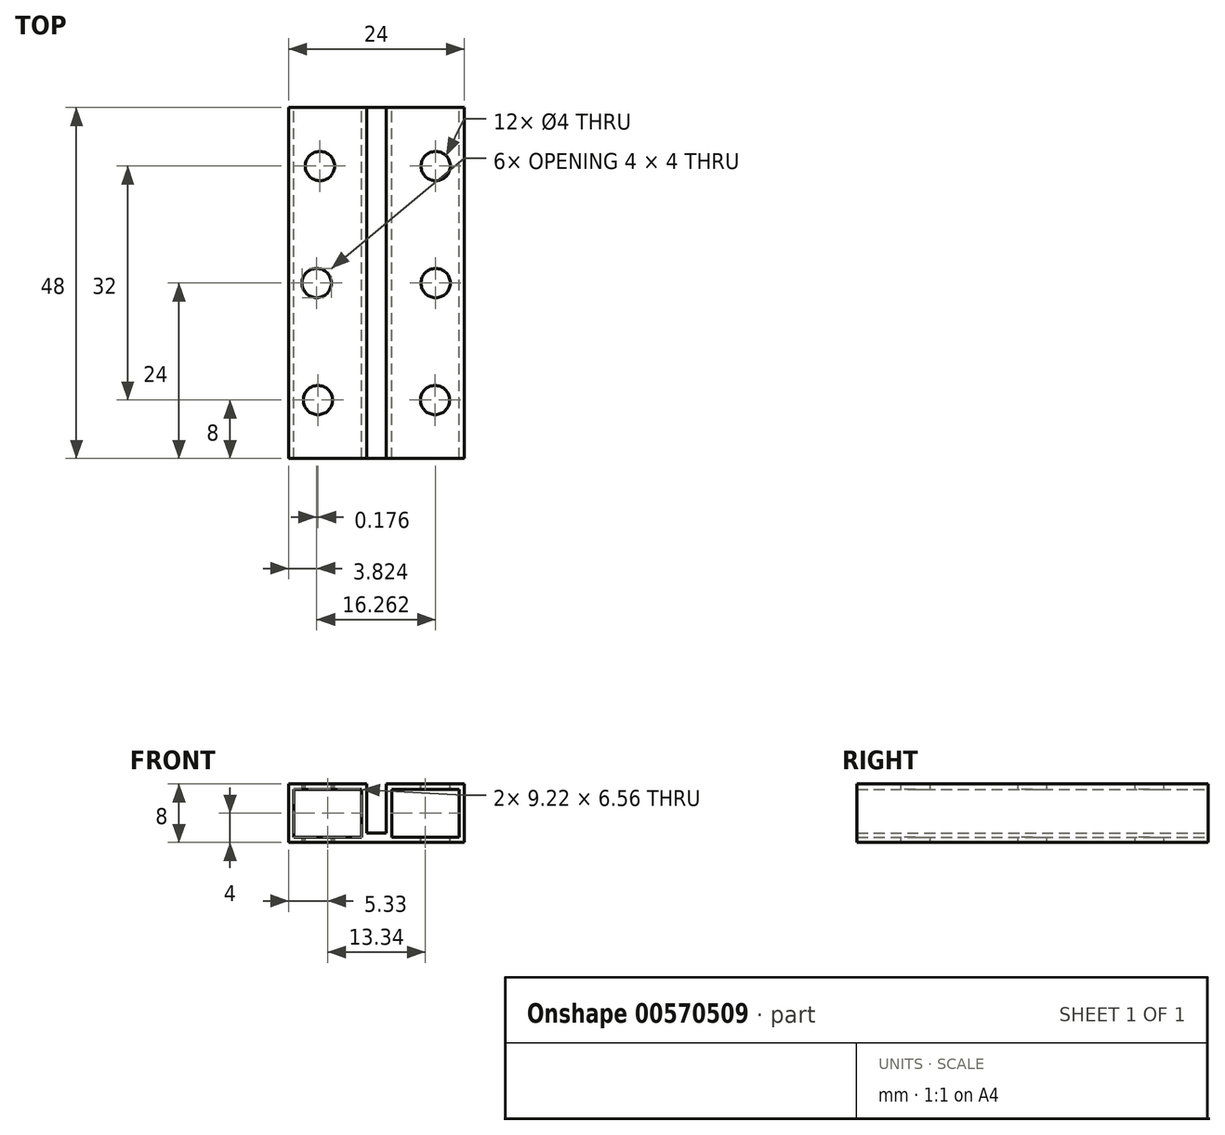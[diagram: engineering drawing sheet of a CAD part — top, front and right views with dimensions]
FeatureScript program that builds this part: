
annotation { "Feature Type Name" : "Feature", "Feature Type Description" : "" }
export const myFeature = defineFeature(function(context is Context, id is Id, definition is map)
    precondition{}
    {
        {
            var Q0;
            Q0=qCreatedBy(makeId("Front.planeOp"),FACE);
            var sketch = newSketch(context, id + "F0", { "sketchPlane" : qUnion([Q0])});
            skLineSegment(sketch, "E0.bottom", {"start": v(-12, 4) * mm, "end": v(12, 4) * mm});
            skLineSegment(sketch, "E0.top", {"start": v(-12, -4) * mm, "end": v(12, -4) * mm});
            skLineSegment(sketch, "E0.left", {"start": v(-12, 4) * mm, "end": v(-12, -4) * mm});
            skLineSegment(sketch, "E0.right", {"start": v(12, 4) * mm, "end": v(12, -4) * mm});
            skPoint(sketch, "E0.middle", {"position": v(0, 0) * mm});
            skLineSegment(sketch, "E1.bottom", {"start": v(-1.34, 10.75) * mm, "end": v(1.34, 10.75) * mm});
            skLineSegment(sketch, "E1.top", {"start": v(-1.34, -2.75) * mm, "end": v(1.34, -2.75) * mm});
            skLineSegment(sketch, "E1.left", {"start": v(-1.34, 10.75) * mm, "end": v(-1.34, -2.75) * mm});
            skLineSegment(sketch, "E1.right", {"start": v(1.34, 10.75) * mm, "end": v(1.34, -2.75) * mm});
            skPoint(sketch, "E1.middle", {"position": v(0, 4) * mm});
            skLineSegment(sketch, "E2.bottom", {"start": v(11.28, -3.28) * mm, "end": v(2.06, -3.28) * mm});
            skLineSegment(sketch, "E2.top", {"start": v(11.28, 3.28) * mm, "end": v(2.06, 3.28) * mm});
            skLineSegment(sketch, "E2.left", {"start": v(11.28, -3.28) * mm, "end": v(11.28, 3.28) * mm});
            skLineSegment(sketch, "E2.right", {"start": v(2.06, -3.28) * mm, "end": v(2.06, 3.28) * mm});
            skLineSegment(sketch, "E3.bottom", {"start": v(-2.06, 3.28) * mm, "end": v(-11.28, 3.28) * mm});
            skLineSegment(sketch, "E3.top", {"start": v(-2.06, -3.28) * mm, "end": v(-11.28, -3.28) * mm});
            skLineSegment(sketch, "E3.left", {"start": v(-2.06, 3.28) * mm, "end": v(-2.06, -3.28) * mm});
            skLineSegment(sketch, "E3.right", {"start": v(-11.28, 3.28) * mm, "end": v(-11.28, -3.28) * mm});
            skLineSegment(sketch, "E4.bottom", {"start": v(-9.78, 3.28) * mm, "end": v(-6.31, 3.28) * mm});
            skLineSegment(sketch, "E4.top", {"start": v(-9.78, -3.28) * mm, "end": v(-6.31, -3.28) * mm});
            skLineSegment(sketch, "E4.left", {"start": v(-9.78, 3.28) * mm, "end": v(-9.78, -3.28) * mm});
            skLineSegment(sketch, "E4.right", {"start": v(-6.31, 3.28) * mm, "end": v(-6.31, -3.28) * mm});
            skLineSegment(sketch, "E5.bottom", {"start": v(6.31, 3.28) * mm, "end": v(9.78, 3.28) * mm});
            skLineSegment(sketch, "E5.top", {"start": v(6.31, -3.28) * mm, "end": v(9.78, -3.28) * mm});
            skLineSegment(sketch, "E5.left", {"start": v(6.31, 3.28) * mm, "end": v(6.31, -3.28) * mm});
            skLineSegment(sketch, "E5.right", {"start": v(9.78, 3.28) * mm, "end": v(9.78, -3.28) * mm});
            skCircle(sketch, "E6", {"center": v(-8, 0) * mm, "radius": 2.16 * mm});
            skCircle(sketch, "E7", {"center": v(8, 0) * mm, "radius": 2.16 * mm});
            skSolve(sketch);
        }
        {
            var Q0;
            Q0=makeQuery(id+"F0.imprint","IMPRINT",FACE,{"disambiguationData":[TD([[makeQuery(id+"F0.imprint","IMPRINT",EDGE,{"derivedFrom":sQuery(id+"F0.wireOp",EDGE,"E0.top")}),1.0]])]});
            var Q1;
            {var subQ0=sQuery(id+"F0.wireOp",EDGE,"E4.bottom");Q1=makeQuery(id+"F0.imprint","IMPRINT",FACE,{"disambiguationData":[TD([[makeQuery(id+"F0.imprint","IMPRINT",EDGE,{"derivedFrom":subQ0}),-1.0]])]});}
            var Q2;
            {var subQ0=sQuery(id+"F0.wireOp",EDGE,"E4.top");Q2=makeQuery(id+"F0.imprint","IMPRINT",FACE,{"disambiguationData":[TD([[makeQuery(id+"F0.imprint","IMPRINT",EDGE,{"derivedFrom":subQ0}),1.0]])]});}
            var Q3;
            {var subQ0=sQuery(id+"F0.wireOp",EDGE,"E5.bottom");Q3=makeQuery(id+"F0.imprint","IMPRINT",FACE,{"disambiguationData":[TD([[makeQuery(id+"F0.imprint","IMPRINT",EDGE,{"derivedFrom":subQ0}),-1.0]])]});}
            var Q4;
            {var subQ0=sQuery(id+"F0.wireOp",EDGE,"E5.top");Q4=makeQuery(id+"F0.imprint","IMPRINT",FACE,{"disambiguationData":[TD([[makeQuery(id+"F0.imprint","IMPRINT",EDGE,{"derivedFrom":subQ0}),1.0]])]});}
            extrude(context, id + "F1", {"entities" : qUnion([Q0, Q1, Q2, Q3, Q4]), "depth" : 48 * mm, "offsetDistance" : 25 * mm});
        }
        {
            var Q0;
            {var subQ0=sQuery(id+"F0.wireOp",EDGE,"E0.bottom");Q0=makeQuery(id+"F1.opExtrude","SWEPT_FACE",FACE,{"disambiguationData":[OSD([subQ0]),TDD([makeQuery(id+"F0.imprint","IMPRINT",EDGE,{"disambiguationData":[TD([[makeQuery(id+"F0.imprint","INTERSECT",VERTEX,{"derivedFrom":[subQ0,sQuery(id+"F0.wireOp",EDGE,"E0.right")]}),1.0]])],"derivedFrom":subQ0})])]});}
            var sketch = newSketch(context, id + "F2", { "sketchPlane" : qUnion([Q0])});
            skCircle(sketch, "E8", {"center": v(8, -40) * mm, "radius": 2 * mm});
            skCircle(sketch, "E9", {"center": v(-8, -40) * mm, "radius": 2 * mm});
            skCircle(sketch, "E10", {"center": v(8.09, -24) * mm, "radius": 2 * mm});
            skCircle(sketch, "E11", {"center": v(-8.18, -24) * mm, "radius": 2 * mm});
            skCircle(sketch, "E12", {"center": v(8.09, -8) * mm, "radius": 2 * mm});
            skCircle(sketch, "E13", {"center": v(-7.73, -8) * mm, "radius": 2 * mm});
            skSolve(sketch);
        }
        {
            var Q0;
            Q0=makeQuery(id+"F2.imprint","IMPRINT",FACE,{"disambiguationData":[TD([[makeQuery(id+"F2.imprint","IMPRINT",EDGE,{"derivedFrom":sQuery(id+"F2.wireOp",EDGE,"E9")}),1.0]])]});
            var Q1;
            Q1=makeQuery(id+"F2.imprint","IMPRINT",FACE,{"disambiguationData":[TD([[makeQuery(id+"F2.imprint","IMPRINT",EDGE,{"derivedFrom":sQuery(id+"F2.wireOp",EDGE,"E8")}),1.0]])]});
            var Q2;
            Q2=makeQuery(id+"F2.imprint","IMPRINT",FACE,{"disambiguationData":[TD([[makeQuery(id+"F2.imprint","IMPRINT",EDGE,{"derivedFrom":sQuery(id+"F2.wireOp",EDGE,"E11")}),1.0]])]});
            var Q3;
            Q3=makeQuery(id+"F2.imprint","IMPRINT",FACE,{"disambiguationData":[TD([[makeQuery(id+"F2.imprint","IMPRINT",EDGE,{"derivedFrom":sQuery(id+"F2.wireOp",EDGE,"E10")}),1.0]])]});
            var Q4;
            Q4=makeQuery(id+"F2.imprint","IMPRINT",FACE,{"disambiguationData":[TD([[makeQuery(id+"F2.imprint","IMPRINT",EDGE,{"derivedFrom":sQuery(id+"F2.wireOp",EDGE,"E13")}),1.0]])]});
            var Q5;
            Q5=makeQuery(id+"F2.imprint","IMPRINT",FACE,{"disambiguationData":[TD([[makeQuery(id+"F2.imprint","IMPRINT",EDGE,{"derivedFrom":sQuery(id+"F2.wireOp",EDGE,"E12")}),1.0]])]});
            extrude(context, id + "F3", {"entities" : qUnion([Q0, Q1, Q2, Q3, Q4, Q5]), "operationType" : NewBodyOperationType.REMOVE, "oppositeDirection" : true, "depth" : 8.1 * mm, "offsetDistance" : 25 * mm});
        }
    });
